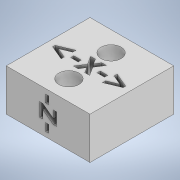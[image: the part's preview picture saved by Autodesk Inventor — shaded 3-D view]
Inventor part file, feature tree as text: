
AUTODESK INVENTOR PART (.ipt)
format: ipt  version: 2020.3 (Build 243373000, 373)  size: 181,248 bytes
history: native  units: in
note: dims shown in document units (in); Inventor stores cm internally (conversion verified against a paired STEP export)
features: extrude x4, sketch x4
ambient origin geometry x8: Origin, YZ Plane, XZ Plane, XY Plane, X Axis, Y Axis, Z Axis, Center Point
bodies: Solid1 (feature_tree)
feature tree (8):
  extrude  "Extrusion1"  Depth=0.9843in
  extrude  "Extrusion2"  Depth=0.2in TaperAngle=0.0deg
  extrude  "Extrusion3"  Depth=0.0063in
  extrude  "Extrusion4"  Depth=0.0063in
  sketch  "Sketch1"  dims[d0=0.9843in d1=0.9843in]
  sketch  "Sketch2"  dims[d2=0.4921in d3=0.0in d4=0.2in d5=0.0in]
  sketch  "Sketch3"  dims[d6=0.2in d7=0.0in d46=0.0063in]
  sketch  "Sketch11"  dims[d48=60.0deg d67=0.0063in d69=60.0deg d81=0.2362in d82=0.2362in d83=0.2362in d84=1.0in d85=0.0in d99=0.0063in d101=60.0deg d120=0.0063in d122=60.0deg d143=0.3779in d161=0.3779in]
